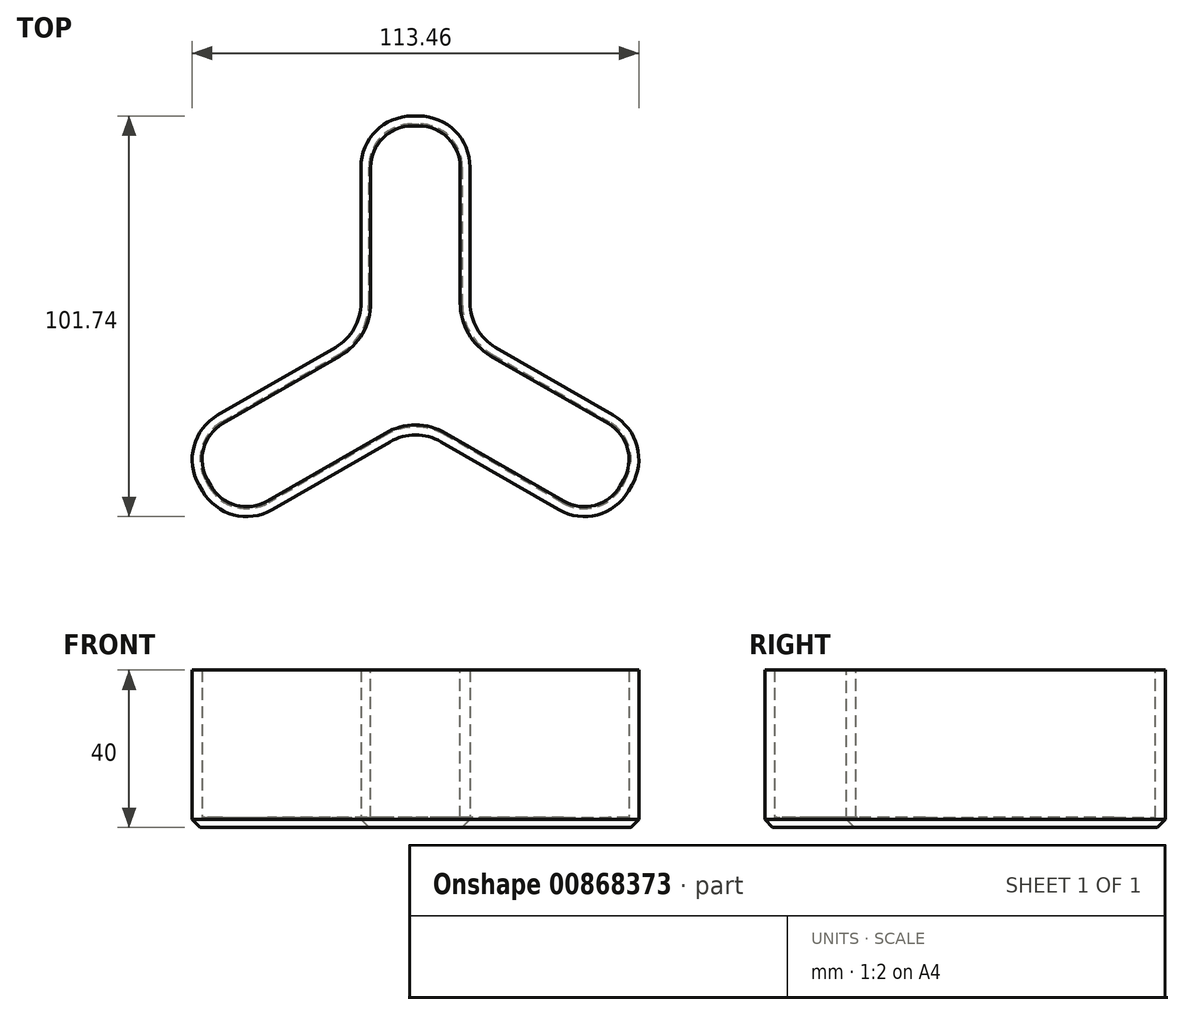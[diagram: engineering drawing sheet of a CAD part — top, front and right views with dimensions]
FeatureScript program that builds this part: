
annotation { "Feature Type Name" : "Feature", "Feature Type Description" : "" }
export const myFeature = defineFeature(function(context is Context, id is Id, definition is map)
    precondition{}
    {
        {
            var Q0;
            Q0=qCreatedBy(makeId("Top.planeOp"),FACE);
            var sketch = newSketch(context, id + "F0", { "sketchPlane" : qUnion([Q0])});
            skCircle(sketch, "E0", {"center": v(0, 0) * mm, "radius": 16 * mm, "construction": true});
            skLineSegment(sketch, "E1", {"start": v(-13.86, 8) * mm, "end": v(-13.86, 63) * mm});
            skLineSegment(sketch, "E2", {"start": v(-13.86, 63) * mm, "end": v(13.86, 63) * mm});
            skLineSegment(sketch, "E3", {"start": v(13.86, 63) * mm, "end": v(13.86, 8) * mm});
            skLineSegment(sketch, "E4.1.0", {"start": v(-47.63, -43.5) * mm, "end": v(-61.49, -19.5) * mm});
            skLineSegment(sketch, "E4.1.1", {"start": v(-61.49, -19.5) * mm, "end": v(-13.86, 8) * mm});
            skLineSegment(sketch, "E4.1.2", {"start": v(0, -16) * mm, "end": v(-47.63, -43.5) * mm});
            skLineSegment(sketch, "E4.2.0", {"start": v(61.49, -19.5) * mm, "end": v(47.63, -43.5) * mm});
            skLineSegment(sketch, "E4.2.1", {"start": v(47.63, -43.5) * mm, "end": v(0, -16) * mm});
            skLineSegment(sketch, "E4.2.2", {"start": v(13.86, 8) * mm, "end": v(61.49, -19.5) * mm});
            skSolve(sketch);
        }
        {
            var Q0;
            Q0=makeQuery(id+"F0.imprint","IMPRINT",FACE,{"disambiguationData":[TD([[makeQuery(id+"F0.imprint","IMPRINT",EDGE,{"derivedFrom":sQuery(id+"F0.wireOp",EDGE,"E1")}),-1.0]])]});
            extrude(context, id + "F1", {"entities" : qUnion([Q0]), "depth" : 40 * mm, "offsetDistance" : 25 * mm});
        }
        {
            var Q0;
            Q0=makeQuery(id+"F1.opExtrude","SWEPT_EDGE",EDGE,{"disambiguationData":[OSD([sQuery(id+"F0.wireOp",EDGE,"E4.1.0"),sQuery(id+"F0.wireOp",EDGE,"E4.1.2")])]});
            var Q1;
            Q1=makeQuery(id+"F1.opExtrude","SWEPT_EDGE",EDGE,{"disambiguationData":[OSD([sQuery(id+"F0.wireOp",EDGE,"E4.1.0"),sQuery(id+"F0.wireOp",EDGE,"E4.1.1")])]});
            var Q2;
            Q2=makeQuery(id+"F1.opExtrude","SWEPT_EDGE",EDGE,{"disambiguationData":[OSD([sQuery(id+"F0.wireOp",EDGE,"E4.1.2"),sQuery(id+"F0.wireOp",EDGE,"E4.2.1")])]});
            var Q3;
            Q3=makeQuery(id+"F1.opExtrude","SWEPT_EDGE",EDGE,{"disambiguationData":[OSD([sQuery(id+"F0.wireOp",EDGE,"E4.2.0"),sQuery(id+"F0.wireOp",EDGE,"E4.2.1")])]});
            var Q4;
            Q4=makeQuery(id+"F1.opExtrude","SWEPT_EDGE",EDGE,{"disambiguationData":[OSD([sQuery(id+"F0.wireOp",EDGE,"E4.2.0"),sQuery(id+"F0.wireOp",EDGE,"E4.2.2")])]});
            var Q5;
            Q5=makeQuery(id+"F1.opExtrude","SWEPT_EDGE",EDGE,{"disambiguationData":[OSD([sQuery(id+"F0.wireOp",EDGE,"E3"),sQuery(id+"F0.wireOp",EDGE,"E4.2.2")])]});
            var Q6;
            Q6=makeQuery(id+"F1.opExtrude","SWEPT_EDGE",EDGE,{"disambiguationData":[OSD([sQuery(id+"F0.wireOp",EDGE,"E2"),sQuery(id+"F0.wireOp",EDGE,"E3")])]});
            var Q7;
            Q7=makeQuery(id+"F1.opExtrude","SWEPT_EDGE",EDGE,{"disambiguationData":[OSD([sQuery(id+"F0.wireOp",EDGE,"E1"),sQuery(id+"F0.wireOp",EDGE,"E2")])]});
            var Q8;
            Q8=makeQuery(id+"F1.opExtrude","SWEPT_EDGE",EDGE,{"disambiguationData":[OSD([sQuery(id+"F0.wireOp",EDGE,"E1"),sQuery(id+"F0.wireOp",EDGE,"E4.1.1")])]});
            fillet(context, id + "F2", {"entities" : qUnion([Q0, Q1, Q2, Q3, Q4, Q5, Q6, Q7, Q8]), "radius" : 13 * mm, "tangentPropagation" : true, "allowEdgeOverflow" : false});
        }
        {
            var Q0;
            Q0=makeQuery(id+"F1.opExtrude","CAP_FACE",FACE,{"disambiguationData":[OSD([sQuery(id+"F0.wireOp",EDGE,"E1"),sQuery(id+"F0.wireOp",EDGE,"E2"),sQuery(id+"F0.wireOp",EDGE,"E3"),sQuery(id+"F0.wireOp",EDGE,"E4.1.0"),sQuery(id+"F0.wireOp",EDGE,"E4.1.1"),sQuery(id+"F0.wireOp",EDGE,"E4.1.2"),sQuery(id+"F0.wireOp",EDGE,"E4.2.0"),sQuery(id+"F0.wireOp",EDGE,"E4.2.1"),sQuery(id+"F0.wireOp",EDGE,"E4.2.2")])],"isStart":false});
            shell(context, id + "F3", {"entities" : qUnion([Q0]), "thickness" : 2.5 * mm});
        }
        {
            var Q0;
            Q0=makeQuery(id+"F1.opExtrude","CAP_FACE",FACE,{"disambiguationData":[OSD([sQuery(id+"F0.wireOp",EDGE,"E1"),sQuery(id+"F0.wireOp",EDGE,"E2"),sQuery(id+"F0.wireOp",EDGE,"E3"),sQuery(id+"F0.wireOp",EDGE,"E4.1.0"),sQuery(id+"F0.wireOp",EDGE,"E4.1.1"),sQuery(id+"F0.wireOp",EDGE,"E4.1.2"),sQuery(id+"F0.wireOp",EDGE,"E4.2.0"),sQuery(id+"F0.wireOp",EDGE,"E4.2.1"),sQuery(id+"F0.wireOp",EDGE,"E4.2.2")])],"isStart":true});
            chamfer(context, id + "F4", {"entities" : qUnion([Q0]), "width" : 2 * mm, "tangentPropagation" : true});
        }
    });
